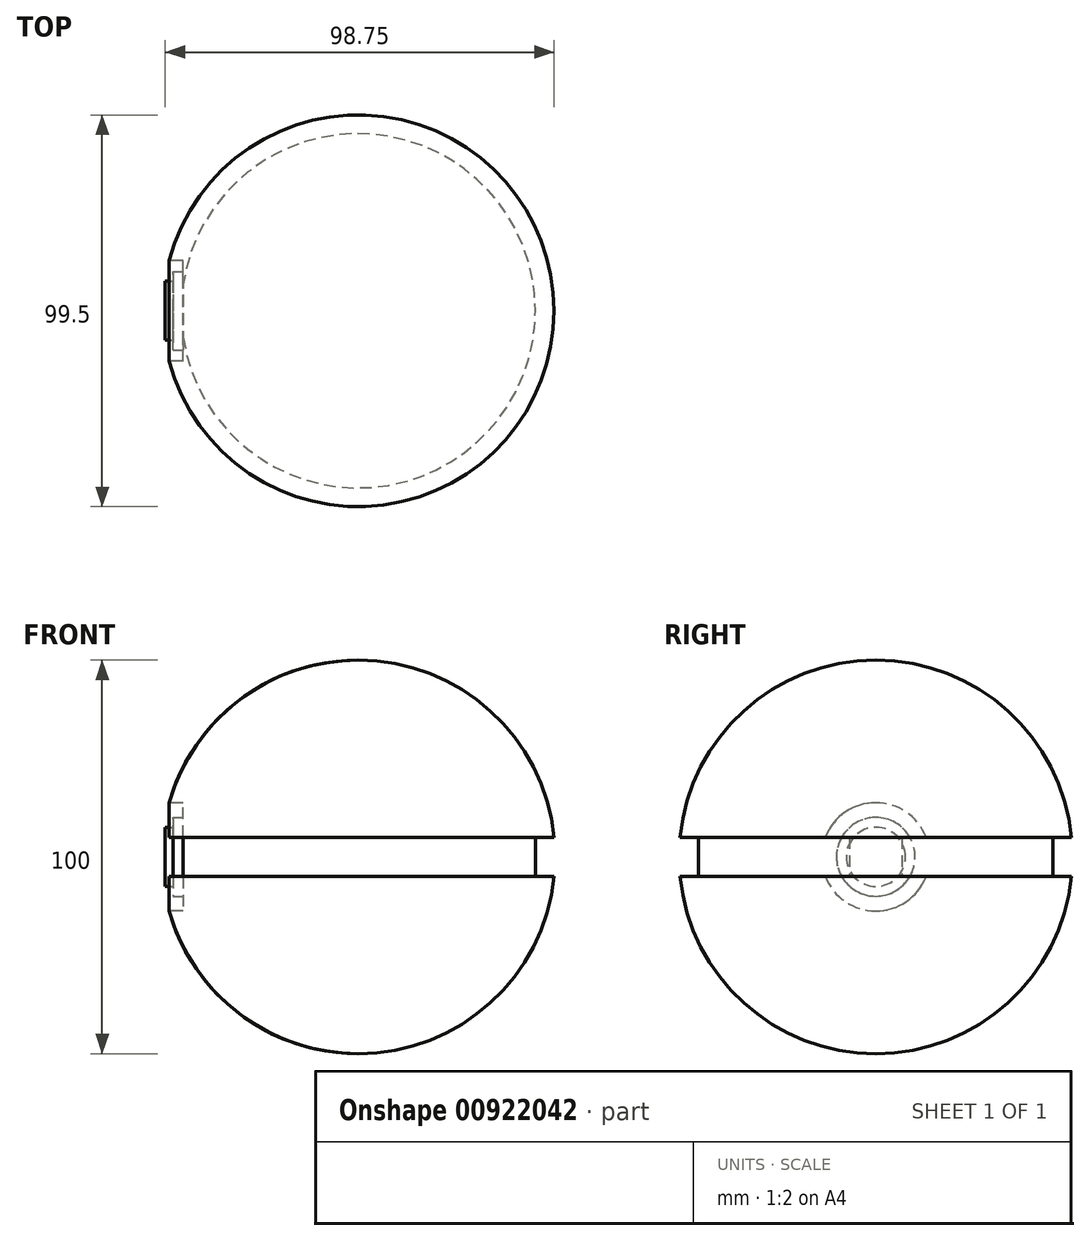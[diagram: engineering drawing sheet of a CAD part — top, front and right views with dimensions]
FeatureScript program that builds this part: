
annotation { "Feature Type Name" : "Feature", "Feature Type Description" : "" }
export const myFeature = defineFeature(function(context is Context, id is Id, definition is map)
    precondition{}
    {
        {
            var Q0;
            Q0=qCreatedBy(makeId("Front.planeOp"),FACE);
            var sketch = newSketch(context, id + "F0", { "sketchPlane" : qUnion([Q0])});
            skArc(sketch, "E0", {"start": v(0, -50) * mm, "mid": v(50, 0) * mm, "end": v(0, 50) * mm});
            skLineSegment(sketch, "E1", {"start": v(0, 50) * mm, "end": v(0, -50) * mm});
            skSolve(sketch);
        }
        {
            var Q0;
            Q0 = qSketchRegion(id + "F0", true);
            var Q1;
            Q1=sQuery(id+"F0.wireOp",EDGE,"E1");
            revolve(context, id + "F1", {"surfaceOperationType" : NewSurfaceOperationType.NEW, "entities" : qUnion([Q0]), "axis" : qUnion([Q1]), "revolveType" : RevolveType.FULL});
        }
        {
            var Q0;
            Q0=qCreatedBy(makeId("Top.planeOp"),FACE);
            var sketch = newSketch(context, id + "F2", { "sketchPlane" : qUnion([Q0])});
            skCircle(sketch, "E2", {"center": v(0, 0) * mm, "radius": 50 * mm});
            skCircle(sketch, "E3", {"center": v(0, 0) * mm, "radius": 45 * mm});
            skSolve(sketch);
        }
        {
            var Q0;
            Q0 = qSketchRegion(id + "F2", true);
            extrude(context, id + "F3", {"entities" : qUnion([Q0]), "operationType" : NewBodyOperationType.REMOVE, "endBound" : BoundingType.SYMMETRIC, "depth" : 10 * mm, "offsetDistance" : 25 * mm});
        }
        {
            var Q0;
            Q0=qCreatedBy(makeId("Right.planeOp"),FACE);
            cPlane(context, id + "F4", {"entities" : qUnion([Q0]), "cplaneType" : CPlaneType.OFFSET, "offset" : 50 * mm, "oppositeDirection" : true, "width" : 150 * mm, "height" : 150 * mm});
        }
        {
            var Q0;
            Q0=qCreatedBy(id+"F4.planeOp",FACE);
            var sketch = newSketch(context, id + "F5", { "sketchPlane" : qUnion([Q0])});
            skCircle(sketch, "E4", {"center": v(0, 0) * mm, "radius": 13.75 * mm});
            skSolve(sketch);
        }
        {
            var Q0;
            Q0 = qSketchRegion(id + "F5", true);
            extrude(context, id + "F6", {"entities" : qUnion([Q0]), "operationType" : NewBodyOperationType.REMOVE, "depth" : 5.5 * mm, "offsetDistance" : 25 * mm});
        }
        {
            var Q0;
            Q0=makeQuery(id+"F6.boolean.opBoolean","COPY",FACE,{"derivedFrom":makeQuery(id+"F6.opExtrude","CAP_FACE",FACE,{"disambiguationData":[OSD([sQuery(id+"F5.wireOp",EDGE,"E4")])],"isStart":false})});
            var sketch = newSketch(context, id + "F7", { "sketchPlane" : qUnion([Q0])});
            skCircle(sketch, "E5", {"center": v(0, 0) * mm, "radius": 10 * mm});
            skSolve(sketch);
        }
        {
            var Q0;
            Q0 = qSketchRegion(id + "F7", true);
            extrude(context, id + "F8", {"entities" : qUnion([Q0]), "operationType" : NewBodyOperationType.ADD, "depth" : 2.5 * mm, "offsetDistance" : 25 * mm});
        }
        {
            var Q0;
            Q0=makeQuery(id+"F8.opExtrude","CAP_FACE",FACE,{"disambiguationData":[OSD([sQuery(id+"F7.wireOp",EDGE,"E5")])],"isStart":false});
            var sketch = newSketch(context, id + "F9", { "sketchPlane" : qUnion([Q0])});
            skCircle(sketch, "E6", {"center": v(0, 0) * mm, "radius": 7.5 * mm});
            skSolve(sketch);
        }
        {
            var Q0;
            Q0 = qSketchRegion(id + "F9", true);
            extrude(context, id + "F10", {"entities" : qUnion([Q0]), "operationType" : NewBodyOperationType.ADD, "depth" : 2 * mm, "offsetDistance" : 25 * mm});
        }
    });
